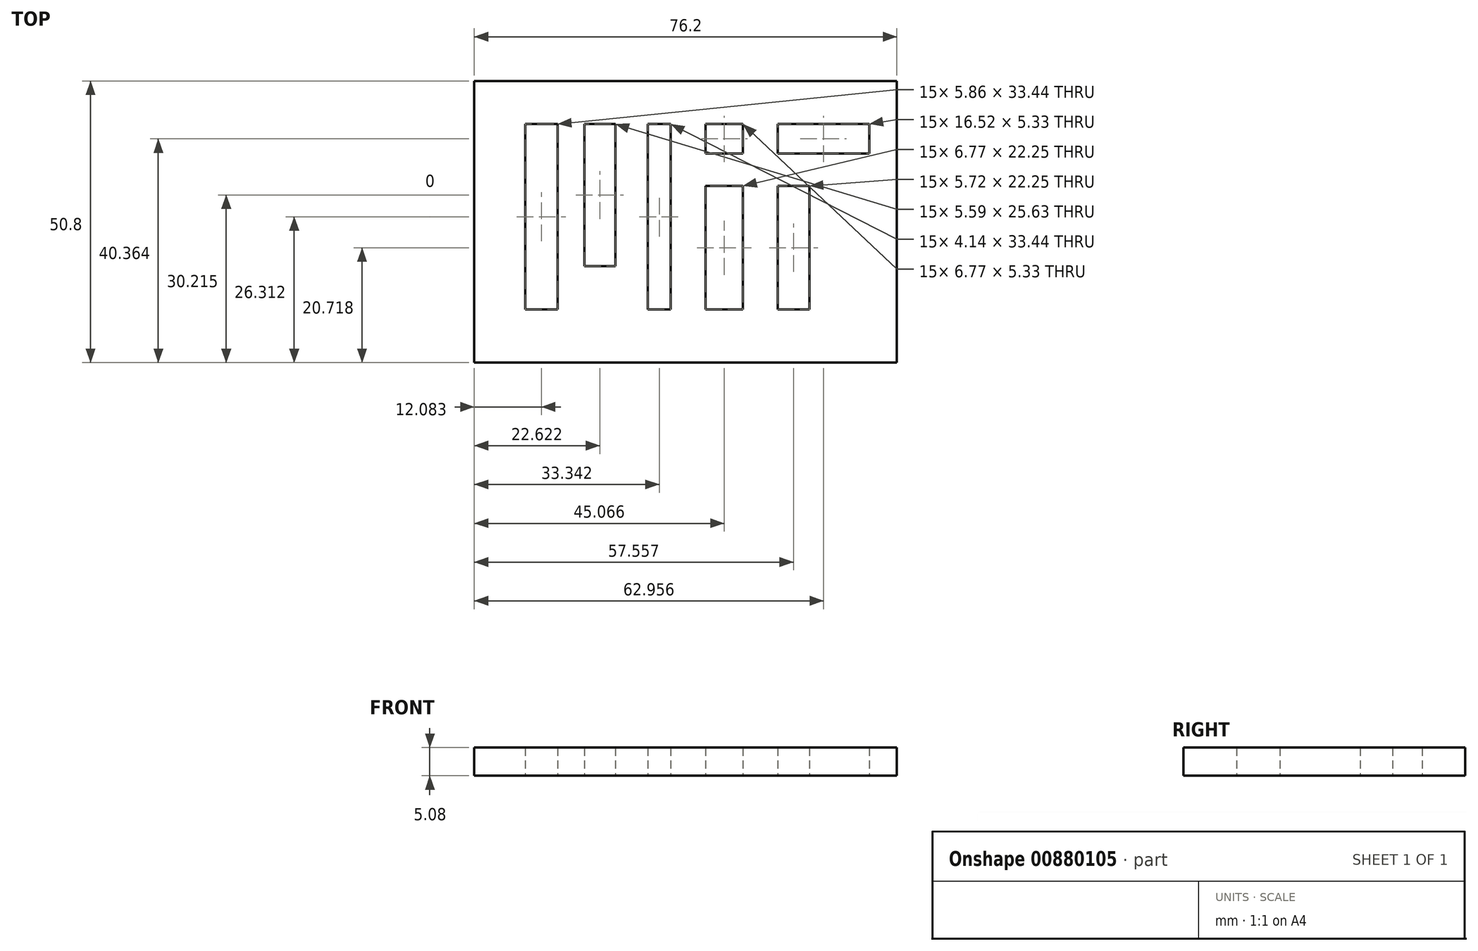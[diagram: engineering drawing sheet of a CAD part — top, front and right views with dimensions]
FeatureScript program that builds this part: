
annotation { "Feature Type Name" : "Feature", "Feature Type Description" : "" }
export const myFeature = defineFeature(function(context is Context, id is Id, definition is map)
    precondition{}
    {
        {
            var Q0;
            Q0=qCreatedBy(makeId("Top.planeOp"),FACE);
            var sketch = newSketch(context, id + "F0", { "sketchPlane" : qUnion([Q0])});
            skLineSegment(sketch, "E0.bottom", {"start": v(-35.41, 21.96) * mm, "end": v(40.79, 21.96) * mm});
            skLineSegment(sketch, "E0.top", {"start": v(-35.41, -28.84) * mm, "end": v(40.79, -28.84) * mm});
            skLineSegment(sketch, "E0.left", {"start": v(-35.41, 21.96) * mm, "end": v(-35.41, -28.84) * mm});
            skLineSegment(sketch, "E0.right", {"start": v(40.79, 21.96) * mm, "end": v(40.79, -28.84) * mm});
            skSolve(sketch);
        }
        {
            var Q0;
            Q0=qCreatedBy(makeId("Top.planeOp"),FACE);
            var sketch = newSketch(context, id + "F1", { "sketchPlane" : qUnion([Q0])});
            skLineSegment(sketch, "E1.bottom", {"start": v(-26.25, 14.2) * mm, "end": v(-20.4, 14.2) * mm});
            skLineSegment(sketch, "E1.top", {"start": v(-26.25, -19.25) * mm, "end": v(-20.4, -19.25) * mm});
            skLineSegment(sketch, "E1.left", {"start": v(-26.25, 14.2) * mm, "end": v(-26.25, -19.25) * mm});
            skLineSegment(sketch, "E1.right", {"start": v(-20.4, 14.2) * mm, "end": v(-20.4, -19.25) * mm});
            skLineSegment(sketch, "E2.bottom", {"start": v(-15.59, 14.2) * mm, "end": v(-10, 14.2) * mm});
            skLineSegment(sketch, "E2.top", {"start": v(-15.59, -11.44) * mm, "end": v(-10, -11.44) * mm});
            skLineSegment(sketch, "E2.left", {"start": v(-15.59, 14.2) * mm, "end": v(-15.59, -11.44) * mm});
            skLineSegment(sketch, "E2.right", {"start": v(-10, 14.2) * mm, "end": v(-10, -11.44) * mm});
            skLineSegment(sketch, "E3.bottom", {"start": v(-4.14, 14.2) * mm, "end": v(0, 14.2) * mm});
            skLineSegment(sketch, "E3.top", {"start": v(-4.14, -19.25) * mm, "end": v(0, -19.25) * mm});
            skLineSegment(sketch, "E3.left", {"start": v(-4.14, 14.2) * mm, "end": v(-4.14, -19.25) * mm});
            skLineSegment(sketch, "E3.right", {"start": v(0, 14.2) * mm, "end": v(0, -19.25) * mm});
            skLineSegment(sketch, "E4.bottom", {"start": v(6.27, 14.2) * mm, "end": v(13.04, 14.2) * mm});
            skLineSegment(sketch, "E4.top", {"start": v(6.27, 8.86) * mm, "end": v(13.04, 8.86) * mm});
            skLineSegment(sketch, "E4.left", {"start": v(6.27, 14.2) * mm, "end": v(6.27, 8.86) * mm});
            skLineSegment(sketch, "E4.right", {"start": v(13.04, 14.2) * mm, "end": v(13.04, 8.86) * mm});
            skLineSegment(sketch, "E5.bottom", {"start": v(6.27, 3) * mm, "end": v(13.04, 3) * mm});
            skLineSegment(sketch, "E5.top", {"start": v(6.27, -19.25) * mm, "end": v(13.04, -19.25) * mm});
            skLineSegment(sketch, "E5.left", {"start": v(6.27, 3) * mm, "end": v(6.27, -19.25) * mm});
            skLineSegment(sketch, "E5.right", {"start": v(13.04, 3) * mm, "end": v(13.04, -19.25) * mm});
            skLineSegment(sketch, "E6.bottom", {"start": v(19.28, 14.2) * mm, "end": v(35.8, 14.2) * mm});
            skLineSegment(sketch, "E6.top", {"start": v(19.28, 8.86) * mm, "end": v(35.8, 8.86) * mm});
            skLineSegment(sketch, "E6.left", {"start": v(19.28, 14.2) * mm, "end": v(19.28, 8.86) * mm});
            skLineSegment(sketch, "E6.right", {"start": v(35.8, 14.2) * mm, "end": v(35.8, 8.86) * mm});
            skLineSegment(sketch, "E7.bottom", {"start": v(19.28, 3) * mm, "end": v(25, 3) * mm});
            skLineSegment(sketch, "E7.top", {"start": v(19.28, -19.25) * mm, "end": v(25, -19.25) * mm});
            skLineSegment(sketch, "E7.left", {"start": v(19.28, 3) * mm, "end": v(19.28, -19.25) * mm});
            skLineSegment(sketch, "E7.right", {"start": v(25, 3) * mm, "end": v(25, -19.25) * mm});
            skSolve(sketch);
        }
        {
            var Q0;
            Q0=makeQuery(id+"F0.imprint","IMPRINT",FACE,{"disambiguationData":[TD([[makeQuery(id+"F0.imprint","IMPRINT",EDGE,{"derivedFrom":sQuery(id+"F0.wireOp",EDGE,"E0.bottom")}),-1.0]])]});
            extrude(context, id + "F2", {"entities" : qUnion([Q0]), "depth" : 5.08 * mm, "offsetDistance" : 25.4 * mm});
        }
        {
            var Q0;
            Q0 = qSketchRegion(id + "F1", true);
            extrude(context, id + "F3", {"entities" : qUnion([Q0]), "depth" : 5.08 * mm, "offsetDistance" : 25.4 * mm});
        }
        {
            var Q0;
            Q0=makeQuery(id+"F3.opExtrude","SWEPT_BODY",BODY,{"disambiguationData":[OSD([sQuery(id+"F1.wireOp",EDGE,"E1.bottom"),sQuery(id+"F1.wireOp",EDGE,"E1.top"),sQuery(id+"F1.wireOp",EDGE,"E1.left"),sQuery(id+"F1.wireOp",EDGE,"E1.right")])]});
            var Q1;
            Q1=makeQuery(id+"F3.opExtrude","SWEPT_BODY",BODY,{"disambiguationData":[OSD([sQuery(id+"F1.wireOp",EDGE,"E7.bottom"),sQuery(id+"F1.wireOp",EDGE,"E7.top"),sQuery(id+"F1.wireOp",EDGE,"E7.left"),sQuery(id+"F1.wireOp",EDGE,"E7.right")])]});
            var Q2;
            Q2=makeQuery(id+"F3.opExtrude","SWEPT_BODY",BODY,{"disambiguationData":[OSD([sQuery(id+"F1.wireOp",EDGE,"E2.bottom"),sQuery(id+"F1.wireOp",EDGE,"E2.top"),sQuery(id+"F1.wireOp",EDGE,"E2.left"),sQuery(id+"F1.wireOp",EDGE,"E2.right")])]});
            var Q3;
            Q3=makeQuery(id+"F3.opExtrude","SWEPT_BODY",BODY,{"disambiguationData":[OSD([sQuery(id+"F1.wireOp",EDGE,"E3.bottom"),sQuery(id+"F1.wireOp",EDGE,"E3.top"),sQuery(id+"F1.wireOp",EDGE,"E3.left"),sQuery(id+"F1.wireOp",EDGE,"E3.right")])]});
            var Q4;
            Q4=makeQuery(id+"F3.opExtrude","SWEPT_BODY",BODY,{"disambiguationData":[OSD([sQuery(id+"F1.wireOp",EDGE,"E4.bottom"),sQuery(id+"F1.wireOp",EDGE,"E4.top"),sQuery(id+"F1.wireOp",EDGE,"E4.left"),sQuery(id+"F1.wireOp",EDGE,"E4.right")])]});
            var Q5;
            Q5=makeQuery(id+"F3.opExtrude","SWEPT_BODY",BODY,{"disambiguationData":[OSD([sQuery(id+"F1.wireOp",EDGE,"E5.bottom"),sQuery(id+"F1.wireOp",EDGE,"E5.top"),sQuery(id+"F1.wireOp",EDGE,"E5.left"),sQuery(id+"F1.wireOp",EDGE,"E5.right")])]});
            var Q6;
            Q6=makeQuery(id+"F3.opExtrude","SWEPT_BODY",BODY,{"disambiguationData":[OSD([sQuery(id+"F1.wireOp",EDGE,"E6.bottom"),sQuery(id+"F1.wireOp",EDGE,"E6.top"),sQuery(id+"F1.wireOp",EDGE,"E6.left"),sQuery(id+"F1.wireOp",EDGE,"E6.right")])]});
            var Q7;
            Q7=makeQuery(id+"F2.opExtrude","SWEPT_BODY",BODY,{"disambiguationData":[OSD([sQuery(id+"F0.wireOp",EDGE,"E0.bottom"),sQuery(id+"F0.wireOp",EDGE,"E0.top"),sQuery(id+"F0.wireOp",EDGE,"E0.left"),sQuery(id+"F0.wireOp",EDGE,"E0.right")])]});
            booleanBodies(context, id + "F4", {"operationType" : BooleanOperationType.SUBTRACTION, "tools" : qUnion([Q0, Q1, Q2, Q3, Q4, Q5, Q6]), "targets" : qUnion([Q7]), "keepTools" : true});
        }
    });
